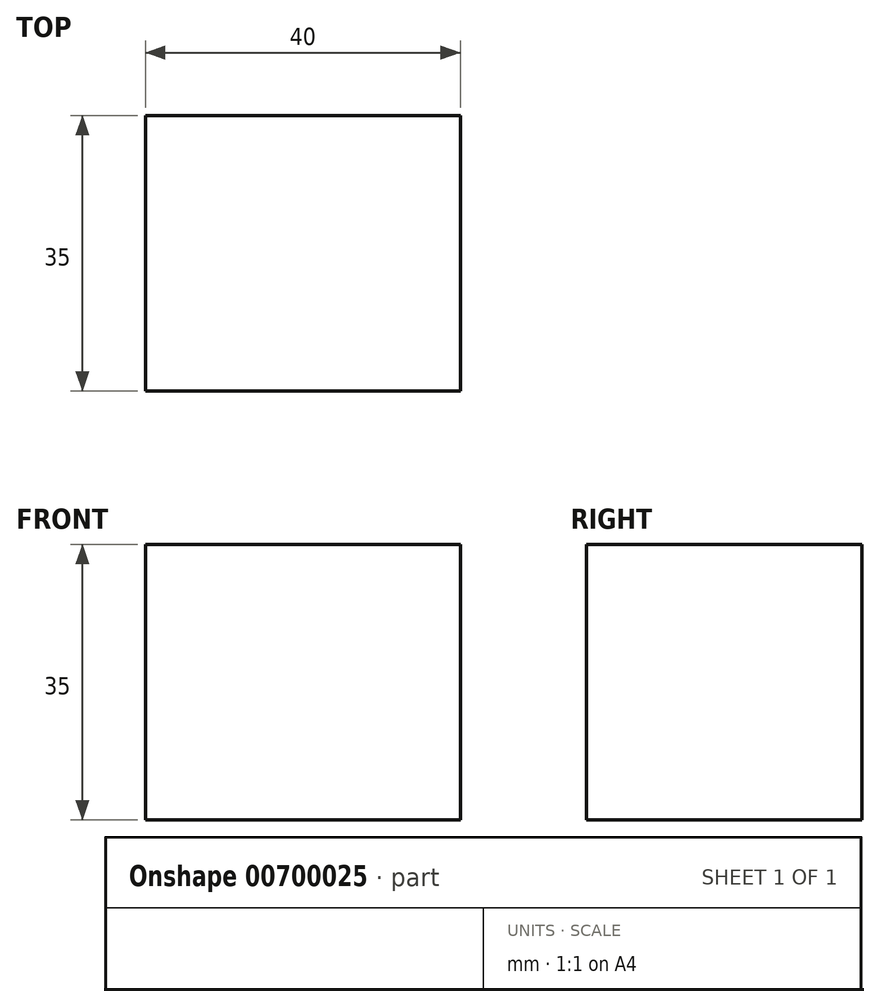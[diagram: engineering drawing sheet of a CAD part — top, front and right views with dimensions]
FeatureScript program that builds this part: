
annotation { "Feature Type Name" : "Feature", "Feature Type Description" : "" }
export const myFeature = defineFeature(function(context is Context, id is Id, definition is map)
    precondition{}
    {
        {
            var Q0;
            Q0=qCreatedBy(makeId("Top.planeOp"),FACE);
            var sketch = newSketch(context, id + "F0", { "sketchPlane" : qUnion([Q0])});
            skLineSegment(sketch, "E0.bottom", {"start": v(20, -17.5) * mm, "end": v(-20, -17.5) * mm});
            skLineSegment(sketch, "E0.top", {"start": v(20, 17.5) * mm, "end": v(-20, 17.5) * mm});
            skLineSegment(sketch, "E0.left", {"start": v(20, -17.5) * mm, "end": v(20, 17.5) * mm});
            skLineSegment(sketch, "E0.right", {"start": v(-20, -17.5) * mm, "end": v(-20, 17.5) * mm});
            skPoint(sketch, "E0.middle", {"position": v(0, 0) * mm});
            skSolve(sketch);
        }
        {
            var Q0;
            Q0 = qSketchRegion(id + "F0", true);
            extrude(context, id + "F1", {"entities" : qUnion([Q0]), "depth" : 35 * mm, "offsetDistance" : 25 * mm});
        }
    });
